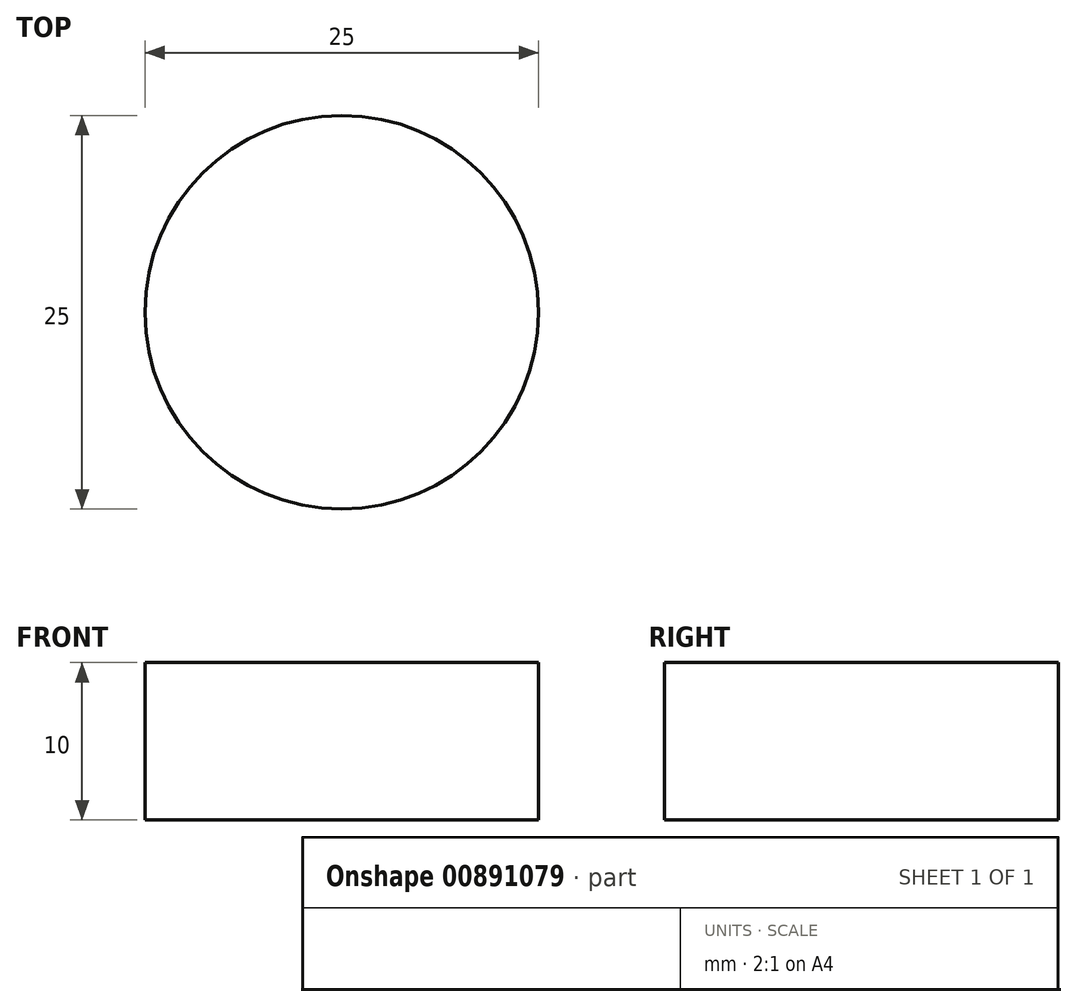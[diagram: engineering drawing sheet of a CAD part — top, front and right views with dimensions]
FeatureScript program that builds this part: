
annotation { "Feature Type Name" : "Feature", "Feature Type Description" : "" }
export const myFeature = defineFeature(function(context is Context, id is Id, definition is map)
    precondition{}
    {
        {
            var Q0;
            Q0=qCreatedBy(makeId("Top.planeOp"),FACE);
            var sketch = newSketch(context, id + "F0", { "sketchPlane" : qUnion([Q0])});
            skCircle(sketch, "E0", {"center": v(0, 0) * mm, "radius": 12.5 * mm});
            skSolve(sketch);
        }
        {
            var Q0;
            Q0 = qSketchRegion(id + "F0", true);
            extrude(context, id + "F1", {"entities" : qUnion([Q0]), "depth" : 10 * mm, "offsetDistance" : 25 * mm});
        }
    });
